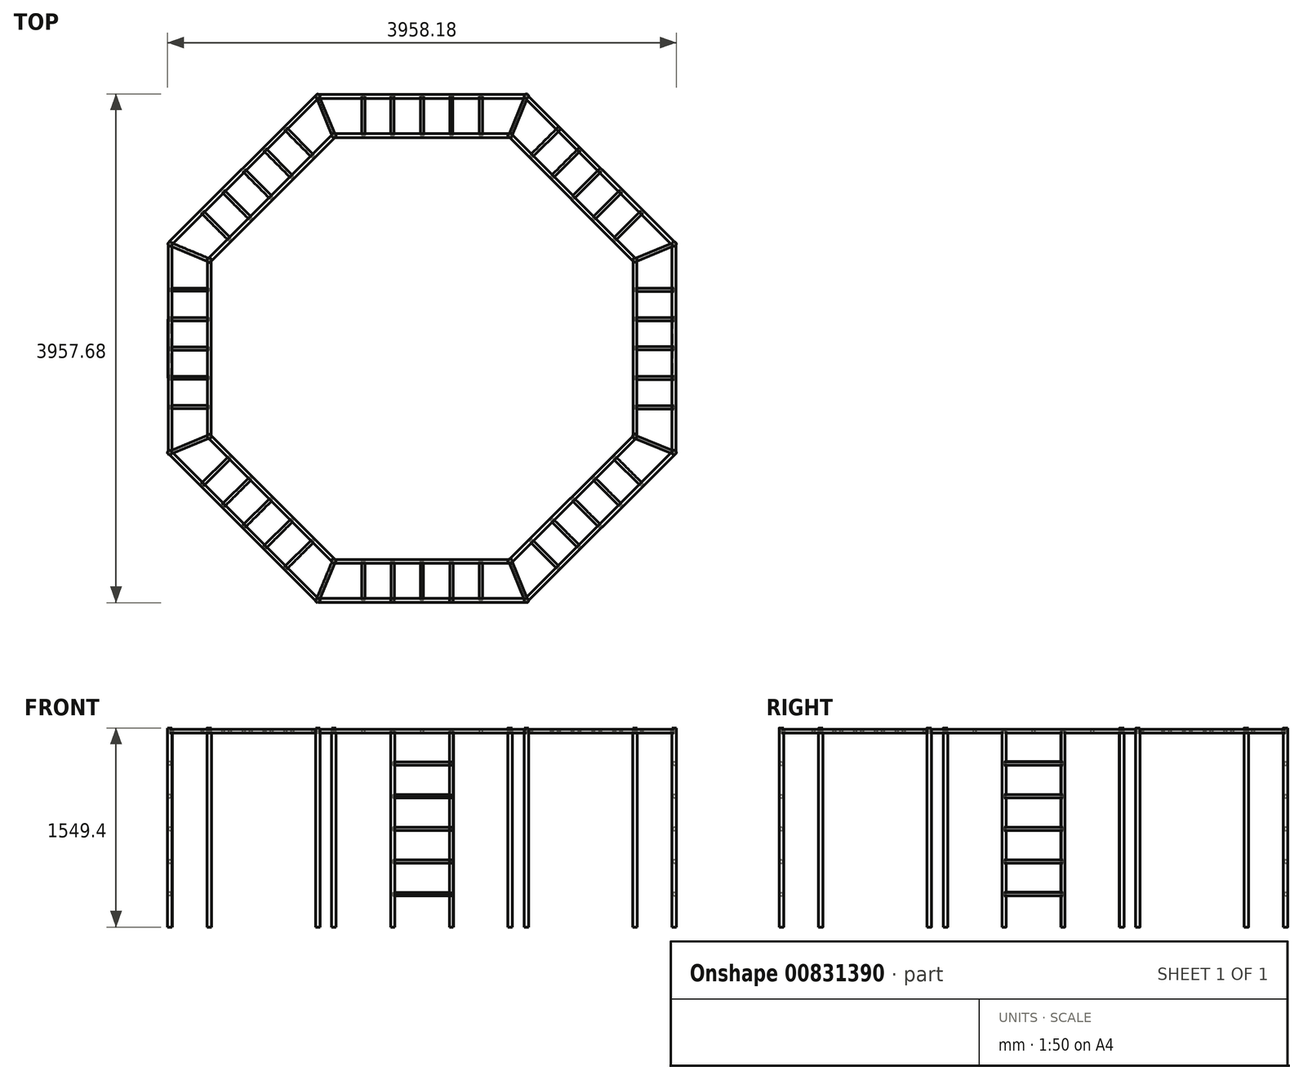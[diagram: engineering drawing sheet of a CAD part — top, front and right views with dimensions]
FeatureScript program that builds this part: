
annotation { "Feature Type Name" : "Feature", "Feature Type Description" : "" }
export const myFeature = defineFeature(function(context is Context, id is Id, definition is map)
    precondition{}
    {
        {
            var Q0;
            Q0=qCreatedBy(makeId("Top.planeOp"),FACE);
            var sketch = newSketch(context, id + "F0", { "sketchPlane" : qUnion([Q0])});
            skLineSegment(sketch, "E0", {"start": v(0, 0) * mm, "end": v(1624.1, 0) * mm});
            skLineSegment(sketch, "E1", {"start": v(1624.1, 0) * mm, "end": v(2772.51, 1148.41) * mm});
            skLineSegment(sketch, "E2", {"start": v(2772.51, 1148.41) * mm, "end": v(2772.51, 2772.51) * mm});
            skLineSegment(sketch, "E3", {"start": v(2772.51, 2772.51) * mm, "end": v(1624.1, 3920.92) * mm});
            skLineSegment(sketch, "E4", {"start": v(1624.1, 3920.92) * mm, "end": v(0, 3920.92) * mm});
            skLineSegment(sketch, "E5", {"start": v(0, 3920.92) * mm, "end": v(-1148.41, 2772.51) * mm});
            skLineSegment(sketch, "E6", {"start": v(-1148.41, 2772.51) * mm, "end": v(-1148.41, 1148.41) * mm});
            skLineSegment(sketch, "E7", {"start": v(-1148.41, 1148.41) * mm, "end": v(0, 0) * mm});
            skLineSegment(sketch, "E8", {"start": v(0, 0) * mm, "end": v(126.25, 304.79) * mm});
            skLineSegment(sketch, "E9", {"start": v(1624.1, 0) * mm, "end": v(1497.85, 304.79) * mm});
            skLineSegment(sketch, "E10", {"start": v(126.25, 304.79) * mm, "end": v(354.85, 304.79) * mm});
            skLineSegment(sketch, "E11", {"start": v(354.85, 304.79) * mm, "end": v(583.45, 304.79) * mm});
            skLineSegment(sketch, "E12", {"start": v(583.45, 304.79) * mm, "end": v(812.05, 304.79) * mm});
            skLineSegment(sketch, "E13", {"start": v(812.05, 304.79) * mm, "end": v(1040.65, 304.79) * mm});
            skLineSegment(sketch, "E14", {"start": v(1040.65, 304.79) * mm, "end": v(1269.25, 304.79) * mm});
            skLineSegment(sketch, "E15", {"start": v(1269.25, 304.79) * mm, "end": v(1497.85, 304.79) * mm});
            skLineSegment(sketch, "E16", {"start": v(354.85, 304.79) * mm, "end": v(354.85, 0) * mm});
            skLineSegment(sketch, "E17", {"start": v(583.45, 304.79) * mm, "end": v(583.45, 0) * mm});
            skLineSegment(sketch, "E18", {"start": v(812.05, 304.79) * mm, "end": v(812.05, 0) * mm});
            skLineSegment(sketch, "E19", {"start": v(1040.65, 304.79) * mm, "end": v(1040.65, 0) * mm});
            skLineSegment(sketch, "E20", {"start": v(1269.25, 304.79) * mm, "end": v(1269.25, 0) * mm});
            skLineSegment(sketch, "E21", {"start": v(2772.51, 1148.41) * mm, "end": v(2467.72, 1274.66) * mm});
            skLineSegment(sketch, "E22", {"start": v(1497.85, 304.79) * mm, "end": v(1659.5, 466.43) * mm});
            skLineSegment(sketch, "E23", {"start": v(1659.5, 466.43) * mm, "end": v(1821.14, 628.08) * mm});
            skLineSegment(sketch, "E24", {"start": v(1821.14, 628.08) * mm, "end": v(1982.79, 789.72) * mm});
            skLineSegment(sketch, "E25", {"start": v(1982.79, 789.72) * mm, "end": v(2144.43, 951.37) * mm});
            skLineSegment(sketch, "E26", {"start": v(2144.43, 951.37) * mm, "end": v(2306.08, 1113.01) * mm});
            skLineSegment(sketch, "E27", {"start": v(2306.08, 1113.01) * mm, "end": v(2467.72, 1274.66) * mm});
            skLineSegment(sketch, "E28", {"start": v(1659.5, 466.43) * mm, "end": v(1875.01, 250.91) * mm});
            skLineSegment(sketch, "E29", {"start": v(1821.14, 628.08) * mm, "end": v(2036.66, 412.56) * mm});
            skLineSegment(sketch, "E30", {"start": v(1982.79, 789.72) * mm, "end": v(2198.3, 574.2) * mm});
            skLineSegment(sketch, "E31", {"start": v(2144.43, 951.37) * mm, "end": v(2359.95, 735.85) * mm});
            skLineSegment(sketch, "E32", {"start": v(2306.08, 1113.01) * mm, "end": v(2521.6, 897.5) * mm});
            skLineSegment(sketch, "E33", {"start": v(2772.51, 2772.51) * mm, "end": v(2467.72, 2646.26) * mm});
            skLineSegment(sketch, "E34", {"start": v(2467.72, 2646.26) * mm, "end": v(2467.72, 2417.66) * mm});
            skLineSegment(sketch, "E35", {"start": v(2467.72, 2417.66) * mm, "end": v(2467.72, 2189.06) * mm});
            skLineSegment(sketch, "E36", {"start": v(2467.72, 2189.06) * mm, "end": v(2467.72, 1960.46) * mm});
            skLineSegment(sketch, "E37", {"start": v(2467.72, 1960.46) * mm, "end": v(2467.72, 1731.86) * mm});
            skLineSegment(sketch, "E38", {"start": v(2467.72, 1731.86) * mm, "end": v(2467.72, 1503.26) * mm});
            skLineSegment(sketch, "E39", {"start": v(2467.72, 1503.26) * mm, "end": v(2467.72, 1274.66) * mm});
            skLineSegment(sketch, "E40", {"start": v(2467.72, 1503.26) * mm, "end": v(2772.51, 1503.26) * mm});
            skLineSegment(sketch, "E41", {"start": v(2467.72, 1731.86) * mm, "end": v(2772.51, 1731.86) * mm});
            skLineSegment(sketch, "E42", {"start": v(2467.72, 1960.46) * mm, "end": v(2772.51, 1960.46) * mm});
            skLineSegment(sketch, "E43", {"start": v(2467.72, 2189.06) * mm, "end": v(2772.51, 2189.06) * mm});
            skLineSegment(sketch, "E44", {"start": v(2467.72, 2417.66) * mm, "end": v(2772.51, 2417.66) * mm});
            skLineSegment(sketch, "E45", {"start": v(1624.1, 3920.92) * mm, "end": v(1497.85, 3616.14) * mm});
            skLineSegment(sketch, "E46", {"start": v(2467.72, 2646.26) * mm, "end": v(2306.08, 2807.9) * mm});
            skLineSegment(sketch, "E47", {"start": v(2306.08, 2807.9) * mm, "end": v(2144.44, 2969.55) * mm});
            skLineSegment(sketch, "E48", {"start": v(2144.44, 2969.55) * mm, "end": v(1982.8, 3131.2) * mm});
            skLineSegment(sketch, "E49", {"start": v(1982.8, 3131.2) * mm, "end": v(1821.15, 3292.84) * mm});
            skLineSegment(sketch, "E50", {"start": v(1821.15, 3292.84) * mm, "end": v(1659.5, 3454.49) * mm});
            skLineSegment(sketch, "E51", {"start": v(1659.5, 3454.49) * mm, "end": v(1497.85, 3616.14) * mm});
            skLineSegment(sketch, "E52", {"start": v(2306.08, 2807.9) * mm, "end": v(2521.6, 3023.43) * mm});
            skLineSegment(sketch, "E53", {"start": v(2144.44, 2969.55) * mm, "end": v(2359.95, 3185.07) * mm});
            skLineSegment(sketch, "E54", {"start": v(1982.8, 3131.2) * mm, "end": v(2198.3, 3346.72) * mm});
            skLineSegment(sketch, "E55", {"start": v(1821.15, 3292.84) * mm, "end": v(2036.66, 3508.36) * mm});
            skLineSegment(sketch, "E56", {"start": v(1659.5, 3454.49) * mm, "end": v(1875.02, 3670) * mm});
            skLineSegment(sketch, "E57.MirrorCS", {"start": v(126.25, 304.79) * mm, "end": v(-35.4, 466.43) * mm});
            skLineSegment(sketch, "E58.MirrorCS", {"start": v(-35.4, 466.43) * mm, "end": v(-250.91, 250.91) * mm});
            skLineSegment(sketch, "E59.MirrorCS", {"start": v(-35.4, 466.43) * mm, "end": v(-197.04, 628.08) * mm});
            skLineSegment(sketch, "E60.MirrorCS", {"start": v(-197.04, 628.08) * mm, "end": v(-358.69, 789.72) * mm});
            skLineSegment(sketch, "E61.MirrorCS", {"start": v(-358.69, 789.72) * mm, "end": v(-520.33, 951.37) * mm});
            skLineSegment(sketch, "E62.MirrorCS", {"start": v(-681.98, 1113.01) * mm, "end": v(-843.62, 1274.66) * mm});
            skLineSegment(sketch, "E63.MirrorCS", {"start": v(-520.33, 951.37) * mm, "end": v(-681.98, 1113.01) * mm});
            skLineSegment(sketch, "E64.MirrorCS", {"start": v(-1148.41, 1148.41) * mm, "end": v(-843.62, 1274.66) * mm});
            skLineSegment(sketch, "E65.MirrorCS", {"start": v(-681.98, 1113.01) * mm, "end": v(-897.5, 897.5) * mm});
            skLineSegment(sketch, "E66.MirrorCS", {"start": v(-520.33, 951.37) * mm, "end": v(-735.85, 735.85) * mm});
            skLineSegment(sketch, "E67.MirrorCS", {"start": v(-358.69, 789.72) * mm, "end": v(-574.2, 574.2) * mm});
            skLineSegment(sketch, "E68.MirrorCS", {"start": v(-197.04, 628.08) * mm, "end": v(-412.56, 412.56) * mm});
            skLineSegment(sketch, "E69.MirrorCS", {"start": v(-843.62, 1274.66) * mm, "end": v(-843.62, 1503.26) * mm});
            skLineSegment(sketch, "E70.MirrorCS", {"start": v(-843.62, 1503.26) * mm, "end": v(-843.62, 1731.86) * mm});
            skLineSegment(sketch, "E71.MirrorCS", {"start": v(-843.62, 1731.86) * mm, "end": v(-843.62, 1960.46) * mm});
            skLineSegment(sketch, "E72.MirrorCS", {"start": v(-843.62, 1960.46) * mm, "end": v(-843.62, 2189.06) * mm});
            skLineSegment(sketch, "E73.MirrorCS", {"start": v(-843.62, 2189.06) * mm, "end": v(-843.62, 2417.66) * mm});
            skLineSegment(sketch, "E74.MirrorCS", {"start": v(-843.62, 2417.66) * mm, "end": v(-843.62, 2646.26) * mm});
            skLineSegment(sketch, "E75.MirrorCS", {"start": v(-1148.41, 2772.51) * mm, "end": v(-843.62, 2646.26) * mm});
            skLineSegment(sketch, "E76.MirrorCS", {"start": v(-843.62, 2417.66) * mm, "end": v(-1148.41, 2417.66) * mm});
            skLineSegment(sketch, "E77.MirrorCS", {"start": v(-843.62, 2189.06) * mm, "end": v(-1148.41, 2189.06) * mm});
            skLineSegment(sketch, "E78.MirrorCS", {"start": v(-843.62, 1960.46) * mm, "end": v(-1148.41, 1960.46) * mm});
            skLineSegment(sketch, "E79.MirrorCS", {"start": v(-843.62, 1731.86) * mm, "end": v(-1148.41, 1731.86) * mm});
            skLineSegment(sketch, "E80.MirrorCS", {"start": v(-843.62, 1503.26) * mm, "end": v(-1148.41, 1503.26) * mm});
            skLineSegment(sketch, "E81.MirrorCS", {"start": v(-681.98, 2807.91) * mm, "end": v(-843.62, 2646.26) * mm});
            skLineSegment(sketch, "E82.MirrorCS", {"start": v(-520.33, 2969.56) * mm, "end": v(-681.98, 2807.91) * mm});
            skLineSegment(sketch, "E83.MirrorCS", {"start": v(-358.69, 3131.2) * mm, "end": v(-520.33, 2969.56) * mm});
            skLineSegment(sketch, "E84.MirrorCS", {"start": v(-197.04, 3292.85) * mm, "end": v(-358.69, 3131.2) * mm});
            skLineSegment(sketch, "E85.MirrorCS", {"start": v(-35.4, 3454.5) * mm, "end": v(-197.04, 3292.85) * mm});
            skLineSegment(sketch, "E86.MirrorCS", {"start": v(126.25, 3616.14) * mm, "end": v(-35.4, 3454.5) * mm});
            skLineSegment(sketch, "E87.MirrorCS", {"start": v(0, 3920.92) * mm, "end": v(126.25, 3616.14) * mm});
            skLineSegment(sketch, "E88.MirrorCS", {"start": v(-35.4, 3454.5) * mm, "end": v(-250.91, 3670) * mm});
            skLineSegment(sketch, "E89.MirrorCS", {"start": v(-197.04, 3292.85) * mm, "end": v(-412.56, 3508.36) * mm});
            skLineSegment(sketch, "E90.MirrorCS", {"start": v(-358.69, 3131.2) * mm, "end": v(-574.2, 3346.72) * mm});
            skLineSegment(sketch, "E91.MirrorCS", {"start": v(-520.33, 2969.56) * mm, "end": v(-735.85, 3185.08) * mm});
            skLineSegment(sketch, "E92.MirrorCS", {"start": v(-681.98, 2807.91) * mm, "end": v(-897.5, 3023.43) * mm});
            skLineSegment(sketch, "E93.MirrorCS", {"start": v(126.25, 3616.14) * mm, "end": v(354.85, 3616.14) * mm});
            skLineSegment(sketch, "E94.MirrorCS", {"start": v(354.85, 3616.14) * mm, "end": v(583.45, 3616.14) * mm});
            skLineSegment(sketch, "E95.MirrorCS", {"start": v(583.45, 3616.14) * mm, "end": v(812.05, 3616.14) * mm});
            skLineSegment(sketch, "E96.MirrorCS", {"start": v(812.05, 3616.14) * mm, "end": v(1040.65, 3616.14) * mm});
            skLineSegment(sketch, "E97.MirrorCS", {"start": v(1040.65, 3616.14) * mm, "end": v(1269.25, 3616.14) * mm});
            skLineSegment(sketch, "E98.MirrorCS", {"start": v(1269.25, 3616.14) * mm, "end": v(1497.85, 3616.14) * mm});
            skLineSegment(sketch, "E99.MirrorCS", {"start": v(1269.25, 3616.14) * mm, "end": v(1269.25, 3920.92) * mm});
            skLineSegment(sketch, "E100.MirrorCS", {"start": v(1040.65, 3616.14) * mm, "end": v(1040.65, 3920.92) * mm});
            skLineSegment(sketch, "E101.MirrorCS", {"start": v(812.05, 3616.14) * mm, "end": v(812.05, 3920.92) * mm});
            skLineSegment(sketch, "E102.MirrorCS", {"start": v(583.45, 3616.14) * mm, "end": v(583.45, 3920.92) * mm});
            skLineSegment(sketch, "E103.MirrorCS", {"start": v(354.85, 3616.14) * mm, "end": v(354.85, 3920.92) * mm});
            skSolve(sketch);
        }
        {
            var Q0;
            Q0=sQuery(id+"F0.wireOp",VERTEX,"E0.start");
            var Q1;
            Q1=sQuery(id+"F0.wireOp",EDGE,"E7");
            cPlane(context, id + "F1", {"entities" : qUnion([Q0, Q1]), "cplaneType" : CPlaneType.LINE_POINT, "offset" : 25.4 * mm, "width" : 152.4 * mm, "height" : 152.4 * mm});
        }
        {
            var Q0;
            Q0=sQuery(id+"F0.wireOp",VERTEX,"E6.end");
            var Q1;
            Q1=sQuery(id+"F0.wireOp",EDGE,"E7");
            cPlane(context, id + "F2", {"entities" : qUnion([Q0, Q1]), "cplaneType" : CPlaneType.LINE_POINT, "offset" : 25.4 * mm, "width" : 152.4 * mm, "height" : 152.4 * mm});
        }
        {
            var Q0;
            Q0=sQuery(id+"F0.wireOp",VERTEX,"E0.end");
            var Q1;
            Q1=sQuery(id+"F0.wireOp",EDGE,"E1");
            cPlane(context, id + "F3", {"entities" : qUnion([Q0, Q1]), "cplaneType" : CPlaneType.LINE_POINT, "offset" : 25.4 * mm, "width" : 152.4 * mm, "height" : 152.4 * mm});
        }
        {
            var Q0;
            Q0=sQuery(id+"F0.wireOp",VERTEX,"E1.end");
            var Q1;
            Q1=sQuery(id+"F0.wireOp",EDGE,"E1");
            cPlane(context, id + "F4", {"entities" : qUnion([Q0, Q1]), "cplaneType" : CPlaneType.LINE_POINT, "offset" : 25.4 * mm, "width" : 152.4 * mm, "height" : 152.4 * mm});
        }
        {
            var Q0;
            Q0=sQuery(id+"F0.wireOp",VERTEX,"E71.MirrorCS.end");
            var Q1;
            Q1=sQuery(id+"F0.wireOp",EDGE,"E78.MirrorCS");
            cPlane(context, id + "F5", {"entities" : qUnion([Q0, Q1]), "cplaneType" : CPlaneType.LINE_POINT, "offset" : 25.4 * mm, "width" : 152.4 * mm, "height" : 152.4 * mm});
        }
        {
            var Q0;
            Q0=qCreatedBy(id+"F5.planeOp",FACE);
            var sketch = newSketch(context, id + "F6", { "sketchPlane" : qUnion([Q0])});
            skLineSegment(sketch, "E104", {"start": v(-1274.16, 0) * mm, "end": v(-1274.16, -1524) * mm});
            skLineSegment(sketch, "E105", {"start": v(-2645.18, 0) * mm, "end": v(-2645.18, -1524) * mm});
            skSolve(sketch);
        }
        {
            var Q0;
            Q0=sQuery(id+"F0.wireOp",VERTEX,"E95.MirrorCS.end");
            var Q1;
            Q1=sQuery(id+"F0.wireOp",EDGE,"E101.MirrorCS");
            cPlane(context, id + "F7", {"entities" : qUnion([Q0, Q1]), "cplaneType" : CPlaneType.LINE_POINT, "offset" : 25.4 * mm, "width" : 152.4 * mm, "height" : 152.4 * mm});
        }
        {
            var Q0;
            Q0=sQuery(id+"F0.wireOp",VERTEX,"E12.end");
            var Q1;
            Q1=sQuery(id+"F0.wireOp",EDGE,"E18");
            cPlane(context, id + "F8", {"entities" : qUnion([Q0, Q1]), "cplaneType" : CPlaneType.LINE_POINT, "offset" : 25.4 * mm, "width" : 152.4 * mm, "height" : 152.4 * mm});
        }
        {
            var Q0;
            Q0=sQuery(id+"F0.wireOp",VERTEX,"E36.end");
            var Q1;
            Q1=sQuery(id+"F0.wireOp",EDGE,"E42");
            cPlane(context, id + "F9", {"entities" : qUnion([Q0, Q1]), "cplaneType" : CPlaneType.LINE_POINT, "offset" : 25.4 * mm, "width" : 152.4 * mm, "height" : 152.4 * mm});
        }
        {
            var Q0;
            Q0=sQuery(id+"F0.wireOp",EDGE,"E0");
            cPoint(context, id + "F10", {"entities" : qUnion([Q0]), "parameter" : 0.5});
        }
        {
            var Q0;
            Q0 = qCreatedBy(id + "F10" ,VERTEX);
            var Q1;
            Q1=sQuery(id+"F0.wireOp",EDGE,"E18");
            cPlane(context, id + "F11", {"entities" : qUnion([Q0, Q1]), "cplaneType" : CPlaneType.LINE_POINT, "offset" : 25.4 * mm, "width" : 152.4 * mm, "height" : 152.4 * mm});
        }
        {
            var Q0;
            Q0=sQuery(id+"F0.wireOp",EDGE,"E2");
            cPoint(context, id + "F12", {"entities" : qUnion([Q0]), "parameter" : 0.5});
        }
        {
            var Q0;
            Q0 = qCreatedBy(id + "F12" ,VERTEX);
            var Q1;
            Q1=sQuery(id+"F0.wireOp",EDGE,"E42");
            cPlane(context, id + "F13", {"entities" : qUnion([Q0, Q1]), "cplaneType" : CPlaneType.LINE_POINT, "offset" : 25.4 * mm, "width" : 152.4 * mm, "height" : 152.4 * mm});
        }
        {
            var Q0;
            Q0=sQuery(id+"F0.wireOp",EDGE,"E4");
            cPoint(context, id + "F14", {"entities" : qUnion([Q0]), "parameter" : 0.5});
        }
        {
            var Q0;
            Q0 = qCreatedBy(id + "F14" ,VERTEX);
            var Q1;
            Q1=sQuery(id+"F0.wireOp",EDGE,"E101.MirrorCS");
            cPlane(context, id + "F15", {"entities" : qUnion([Q0, Q1]), "cplaneType" : CPlaneType.LINE_POINT, "offset" : 25.4 * mm, "width" : 152.4 * mm, "height" : 152.4 * mm});
        }
        {
            var Q0;
            Q0=sQuery(id+"F0.wireOp",EDGE,"E6");
            cPoint(context, id + "F16", {"entities" : qUnion([Q0]), "parameter" : 0.5});
        }
        {
            var Q0;
            Q0 = qCreatedBy(id + "F16" ,VERTEX);
            var Q1;
            Q1=sQuery(id+"F0.wireOp",EDGE,"E78.MirrorCS");
            cPlane(context, id + "F17", {"entities" : qUnion([Q0, Q1]), "cplaneType" : CPlaneType.LINE_POINT, "offset" : 25.4 * mm, "width" : 152.4 * mm, "height" : 152.4 * mm});
        }
        {
            var Q0;
            Q0=qCreatedBy(id+"F1.planeOp",FACE);
            var sketch = newSketch(context, id + "F18", { "sketchPlane" : qUnion([Q0])});
            skCircle(sketch, "E106", {"center": v(0, 0) * mm, "radius": 15 * mm});
            skSolve(sketch);
        }
        {
            var Q0;
            Q0=makeQuery(id+"F18.imprint","IMPRINT",FACE,{"disambiguationData":[TD([[makeQuery(id+"F18.imprint","IMPRINT",EDGE,{"derivedFrom":sQuery(id+"F18.wireOp",EDGE,"E106")}),1.0]])]});
            extrude(context, id + "F19", {"entities" : qUnion([Q0]), "oppositeDirection" : true, "depth" : 1624.1 * mm, "offsetDistance" : 25.4 * mm});
        }
        {
            var Q0;
            Q0=qCreatedBy(makeId("Right.planeOp"),FACE);
            var sketch = newSketch(context, id + "F20", { "sketchPlane" : qUnion([Q0])});
            skCircle(sketch, "E107", {"center": v(0, 0) * mm, "radius": 15 * mm});
            skSolve(sketch);
        }
        {
            var Q0;
            Q0=makeQuery(id+"F20.imprint","IMPRINT",FACE,{"disambiguationData":[TD([[makeQuery(id+"F20.imprint","IMPRINT",EDGE,{"derivedFrom":sQuery(id+"F20.wireOp",EDGE,"E107")}),1.0]])]});
            extrude(context, id + "F21", {"entities" : qUnion([Q0]), "operationType" : NewBodyOperationType.ADD, "depth" : 1624.1 * mm, "offsetDistance" : 25.4 * mm});
        }
        {
            var Q0;
            Q0=sQuery(id+"F0.wireOp",VERTEX,"E6.end");
            var Q1;
            Q1=sQuery(id+"F0.wireOp",EDGE,"E6");
            cPlane(context, id + "F22", {"entities" : qUnion([Q0, Q1]), "cplaneType" : CPlaneType.LINE_POINT, "offset" : 25.4 * mm, "width" : 152.4 * mm, "height" : 152.4 * mm});
        }
        {
            var Q0;
            Q0=qCreatedBy(id+"F22.planeOp",FACE);
            var sketch = newSketch(context, id + "F23", { "sketchPlane" : qUnion([Q0])});
            skCircle(sketch, "E108", {"center": v(-1147.47, 0) * mm, "radius": 15 * mm});
            skSolve(sketch);
        }
        {
            var Q0;
            Q0=makeQuery(id+"F23.imprint","IMPRINT",FACE,{"disambiguationData":[TD([[makeQuery(id+"F23.imprint","IMPRINT",EDGE,{"derivedFrom":sQuery(id+"F23.wireOp",EDGE,"E108")}),1.0]])]});
            extrude(context, id + "F24", {"entities" : qUnion([Q0]), "operationType" : NewBodyOperationType.ADD, "oppositeDirection" : true, "depth" : 1624.1 * mm, "offsetDistance" : 25.4 * mm});
        }
        {
            var Q0;
            Q0=sQuery(id+"F0.wireOp",VERTEX,"E5.end");
            var Q1;
            Q1=sQuery(id+"F0.wireOp",EDGE,"E5");
            cPlane(context, id + "F25", {"entities" : qUnion([Q0, Q1]), "cplaneType" : CPlaneType.LINE_POINT, "offset" : 25.4 * mm, "width" : 152.4 * mm, "height" : 152.4 * mm});
        }
        {
            var Q0;
            Q0=qCreatedBy(id+"F25.planeOp",FACE);
            var sketch = newSketch(context, id + "F26", { "sketchPlane" : qUnion([Q0])});
            skCircle(sketch, "E109", {"center": v(-2774.05, 0) * mm, "radius": 15 * mm});
            skSolve(sketch);
        }
        {
            var Q0;
            Q0=makeQuery(id+"F26.imprint","IMPRINT",FACE,{"disambiguationData":[TD([[makeQuery(id+"F26.imprint","IMPRINT",EDGE,{"derivedFrom":sQuery(id+"F26.wireOp",EDGE,"E109")}),1.0]])]});
            extrude(context, id + "F27", {"entities" : qUnion([Q0]), "operationType" : NewBodyOperationType.ADD, "oppositeDirection" : true, "depth" : 1624.1 * mm, "offsetDistance" : 25.4 * mm});
        }
        {
            var Q0;
            Q0=sQuery(id+"F0.wireOp",VERTEX,"E4.end");
            var Q1;
            Q1=sQuery(id+"F0.wireOp",EDGE,"E4");
            cPlane(context, id + "F28", {"entities" : qUnion([Q0, Q1]), "cplaneType" : CPlaneType.LINE_POINT, "offset" : 25.4 * mm, "width" : 152.4 * mm, "height" : 152.4 * mm});
        }
        {
            var Q0;
            Q0=qCreatedBy(id+"F28.planeOp",FACE);
            var sketch = newSketch(context, id + "F29", { "sketchPlane" : qUnion([Q0])});
            skCircle(sketch, "E110", {"center": v(-3920.97, 0) * mm, "radius": 15 * mm});
            skSolve(sketch);
        }
        {
            var Q0;
            Q0=makeQuery(id+"F29.imprint","IMPRINT",FACE,{"disambiguationData":[TD([[makeQuery(id+"F29.imprint","IMPRINT",EDGE,{"derivedFrom":sQuery(id+"F29.wireOp",EDGE,"E110")}),1.0]])]});
            extrude(context, id + "F30", {"entities" : qUnion([Q0]), "operationType" : NewBodyOperationType.ADD, "oppositeDirection" : true, "depth" : 1624.1 * mm, "offsetDistance" : 25.4 * mm});
        }
        {
            var Q0;
            Q0=sQuery(id+"F0.wireOp",VERTEX,"E3.end");
            var Q1;
            Q1=sQuery(id+"F0.wireOp",EDGE,"E3");
            cPlane(context, id + "F31", {"entities" : qUnion([Q0, Q1]), "cplaneType" : CPlaneType.LINE_POINT, "offset" : 25.4 * mm, "width" : 152.4 * mm, "height" : 152.4 * mm});
        }
        {
            var Q0;
            Q0=qCreatedBy(id+"F31.planeOp",FACE);
            var sketch = newSketch(context, id + "F32", { "sketchPlane" : qUnion([Q0])});
            skCircle(sketch, "E111", {"center": v(-3919.06, 0) * mm, "radius": 15 * mm});
            skSolve(sketch);
        }
        {
            var Q0;
            Q0=makeQuery(id+"F32.imprint","IMPRINT",FACE,{"disambiguationData":[TD([[makeQuery(id+"F32.imprint","IMPRINT",EDGE,{"derivedFrom":sQuery(id+"F32.wireOp",EDGE,"E111")}),1.0]])]});
            extrude(context, id + "F33", {"entities" : qUnion([Q0]), "operationType" : NewBodyOperationType.ADD, "oppositeDirection" : true, "depth" : 1624.1 * mm, "offsetDistance" : 25.4 * mm});
        }
        {
            var Q0;
            Q0=sQuery(id+"F0.wireOp",VERTEX,"E2.end");
            var Q1;
            Q1=sQuery(id+"F0.wireOp",EDGE,"E2");
            cPlane(context, id + "F34", {"entities" : qUnion([Q0, Q1]), "cplaneType" : CPlaneType.LINE_POINT, "offset" : 25.4 * mm, "width" : 152.4 * mm, "height" : 152.4 * mm});
        }
        {
            var Q0;
            Q0=qCreatedBy(id+"F34.planeOp",FACE);
            var sketch = newSketch(context, id + "F35", { "sketchPlane" : qUnion([Q0])});
            skCircle(sketch, "E112", {"center": v(-2771.97, 0) * mm, "radius": 15 * mm});
            skSolve(sketch);
        }
        {
            var Q0;
            Q0=makeQuery(id+"F35.imprint","IMPRINT",FACE,{"disambiguationData":[TD([[makeQuery(id+"F35.imprint","IMPRINT",EDGE,{"derivedFrom":sQuery(id+"F35.wireOp",EDGE,"E112")}),1.0]])]});
            extrude(context, id + "F36", {"entities" : qUnion([Q0]), "operationType" : NewBodyOperationType.ADD, "oppositeDirection" : true, "depth" : 1624.1 * mm, "offsetDistance" : 25.4 * mm});
        }
        {
            var Q0;
            Q0=qCreatedBy(id+"F3.planeOp",FACE);
            var sketch = newSketch(context, id + "F37", { "sketchPlane" : qUnion([Q0])});
            skCircle(sketch, "E113", {"center": v(-1146.74, 0) * mm, "radius": 15 * mm});
            skSolve(sketch);
        }
        {
            var Q0;
            Q0=makeQuery(id+"F37.imprint","IMPRINT",FACE,{"disambiguationData":[TD([[makeQuery(id+"F37.imprint","IMPRINT",EDGE,{"derivedFrom":sQuery(id+"F37.wireOp",EDGE,"E113")}),1.0]])]});
            extrude(context, id + "F38", {"entities" : qUnion([Q0]), "operationType" : NewBodyOperationType.ADD, "depth" : 1624.1 * mm, "offsetDistance" : 25.4 * mm});
        }
        {
            var Q0;
            Q0=sQuery(id+"F0.wireOp",VERTEX,"E8.end");
            var Q1;
            Q1=sQuery(id+"F0.wireOp",EDGE,"E57.MirrorCS");
            cPlane(context, id + "F39", {"entities" : qUnion([Q0, Q1]), "cplaneType" : CPlaneType.LINE_POINT, "offset" : 25.4 * mm, "width" : 152.4 * mm, "height" : 152.4 * mm});
        }
        {
            var Q0;
            Q0=qCreatedBy(id+"F39.planeOp",FACE);
            var sketch = newSketch(context, id + "F40", { "sketchPlane" : qUnion([Q0])});
            skCircle(sketch, "E114", {"center": v(-304.82, 0) * mm, "radius": 15 * mm});
            skSolve(sketch);
        }
        {
            var Q0;
            Q0=makeQuery(id+"F40.imprint","IMPRINT",FACE,{"disambiguationData":[TD([[makeQuery(id+"F40.imprint","IMPRINT",EDGE,{"derivedFrom":sQuery(id+"F40.wireOp",EDGE,"E114")}),1.0]])]});
            extrude(context, id + "F41", {"entities" : qUnion([Q0]), "depth" : 1371.6 * mm, "offsetDistance" : 25.4 * mm});
        }
        {
            var Q0;
            Q0=sQuery(id+"F0.wireOp",VERTEX,"E62.MirrorCS.end");
            var Q1;
            Q1=sQuery(id+"F0.wireOp",EDGE,"E69.MirrorCS");
            cPlane(context, id + "F42", {"entities" : qUnion([Q0, Q1]), "cplaneType" : CPlaneType.LINE_POINT, "offset" : 25.4 * mm, "width" : 152.4 * mm, "height" : 152.4 * mm});
        }
        {
            var Q0;
            Q0=qCreatedBy(id+"F42.planeOp",FACE);
            var sketch = newSketch(context, id + "F43", { "sketchPlane" : qUnion([Q0])});
            skCircle(sketch, "E115", {"center": v(843.67, 0) * mm, "radius": 15 * mm});
            skSolve(sketch);
        }
        {
            var Q0;
            Q0=makeQuery(id+"F43.imprint","IMPRINT",FACE,{"disambiguationData":[TD([[makeQuery(id+"F43.imprint","IMPRINT",EDGE,{"derivedFrom":sQuery(id+"F43.wireOp",EDGE,"E115")}),1.0]])]});
            extrude(context, id + "F44", {"entities" : qUnion([Q0]), "operationType" : NewBodyOperationType.ADD, "depth" : 1371.6 * mm, "offsetDistance" : 25.4 * mm});
        }
        {
            var Q0;
            Q0=sQuery(id+"F6.wireOp",VERTEX,"E105.start");
            var Q1;
            Q1=sQuery(id+"F0.wireOp",EDGE,"E81.MirrorCS");
            cPlane(context, id + "F45", {"entities" : qUnion([Q0, Q1]), "cplaneType" : CPlaneType.LINE_POINT, "offset" : 25.4 * mm, "width" : 152.4 * mm, "height" : 152.4 * mm});
        }
        {
            var Q0;
            Q0=qCreatedBy(id+"F45.planeOp",FACE);
            var sketch = newSketch(context, id + "F46", { "sketchPlane" : qUnion([Q0])});
            skCircle(sketch, "E116", {"center": v(-2467.6, 0) * mm, "radius": 15 * mm});
            skSolve(sketch);
        }
        {
            var Q0;
            Q0=makeQuery(id+"F46.imprint","IMPRINT",FACE,{"disambiguationData":[TD([[makeQuery(id+"F46.imprint","IMPRINT",EDGE,{"derivedFrom":sQuery(id+"F46.wireOp",EDGE,"E116")}),1.0]])]});
            extrude(context, id + "F47", {"entities" : qUnion([Q0]), "operationType" : NewBodyOperationType.ADD, "oppositeDirection" : true, "depth" : 1371.6 * mm, "offsetDistance" : 25.4 * mm});
        }
        {
            var Q0;
            Q0=sQuery(id+"F0.wireOp",VERTEX,"E86.MirrorCS.start");
            var Q1;
            Q1=sQuery(id+"F0.wireOp",EDGE,"E93.MirrorCS");
            cPlane(context, id + "F48", {"entities" : qUnion([Q0, Q1]), "cplaneType" : CPlaneType.LINE_POINT, "offset" : 25.4 * mm, "width" : 152.4 * mm, "height" : 152.4 * mm});
        }
        {
            var Q0;
            Q0=qCreatedBy(id+"F48.planeOp",FACE);
            var sketch = newSketch(context, id + "F49", { "sketchPlane" : qUnion([Q0])});
            skCircle(sketch, "E117", {"center": v(3616.57, 0) * mm, "radius": 15 * mm});
            skSolve(sketch);
        }
        {
            var Q0;
            Q0=makeQuery(id+"F49.imprint","IMPRINT",FACE,{"disambiguationData":[TD([[makeQuery(id+"F49.imprint","IMPRINT",EDGE,{"derivedFrom":sQuery(id+"F49.wireOp",EDGE,"E117")}),1.0]])]});
            extrude(context, id + "F50", {"entities" : qUnion([Q0]), "operationType" : NewBodyOperationType.ADD, "depth" : 1371.6 * mm, "offsetDistance" : 25.4 * mm});
        }
        {
            var Q0;
            Q0=sQuery(id+"F0.wireOp",VERTEX,"E45.end");
            var Q1;
            Q1=sQuery(id+"F0.wireOp",EDGE,"E51");
            cPlane(context, id + "F51", {"entities" : qUnion([Q0, Q1]), "cplaneType" : CPlaneType.LINE_POINT, "offset" : 25.4 * mm, "width" : 152.4 * mm, "height" : 152.4 * mm});
        }
        {
            var Q0;
            Q0=qCreatedBy(id+"F51.planeOp",FACE);
            var sketch = newSketch(context, id + "F52", { "sketchPlane" : qUnion([Q0])});
            skCircle(sketch, "E118", {"center": v(-3616.84, 0) * mm, "radius": 15 * mm});
            skSolve(sketch);
        }
        {
            var Q0;
            Q0=makeQuery(id+"F52.imprint","IMPRINT",FACE,{"disambiguationData":[TD([[makeQuery(id+"F52.imprint","IMPRINT",EDGE,{"derivedFrom":sQuery(id+"F52.wireOp",EDGE,"E118")}),1.0]])]});
            extrude(context, id + "F53", {"entities" : qUnion([Q0]), "operationType" : NewBodyOperationType.ADD, "oppositeDirection" : true, "depth" : 1371.6 * mm, "offsetDistance" : 25.4 * mm});
        }
        {
            var Q0;
            Q0=sQuery(id+"F0.wireOp",VERTEX,"E33.end");
            var Q1;
            Q1=sQuery(id+"F0.wireOp",EDGE,"E34");
            cPlane(context, id + "F54", {"entities" : qUnion([Q0, Q1]), "cplaneType" : CPlaneType.LINE_POINT, "offset" : 25.4 * mm, "width" : 152.4 * mm, "height" : 152.4 * mm});
        }
        {
            var Q0;
            Q0=qCreatedBy(id+"F54.planeOp",FACE);
            var sketch = newSketch(context, id + "F55", { "sketchPlane" : qUnion([Q0])});
            skCircle(sketch, "E119", {"center": v(2468.86, 0) * mm, "radius": 15 * mm});
            skSolve(sketch);
        }
        {
            var Q0;
            Q0=makeQuery(id+"F55.imprint","IMPRINT",FACE,{"disambiguationData":[TD([[makeQuery(id+"F55.imprint","IMPRINT",EDGE,{"derivedFrom":sQuery(id+"F55.wireOp",EDGE,"E119")}),1.0]])]});
            extrude(context, id + "F56", {"entities" : qUnion([Q0]), "operationType" : NewBodyOperationType.ADD, "depth" : 1371.6 * mm, "offsetDistance" : 25.4 * mm});
        }
        {
            var Q0;
            Q0=sQuery(id+"F0.wireOp",VERTEX,"E21.end");
            var Q1;
            Q1=sQuery(id+"F0.wireOp",EDGE,"E27");
            cPlane(context, id + "F57", {"entities" : qUnion([Q0, Q1]), "cplaneType" : CPlaneType.LINE_POINT, "offset" : 25.4 * mm, "width" : 152.4 * mm, "height" : 152.4 * mm});
        }
        {
            var Q0;
            Q0=qCreatedBy(id+"F57.planeOp",FACE);
            var sketch = newSketch(context, id + "F58", { "sketchPlane" : qUnion([Q0])});
            skCircle(sketch, "E120", {"center": v(-843.77, 0) * mm, "radius": 15 * mm});
            skSolve(sketch);
        }
        {
            var Q0;
            Q0=makeQuery(id+"F58.imprint","IMPRINT",FACE,{"disambiguationData":[TD([[makeQuery(id+"F58.imprint","IMPRINT",EDGE,{"derivedFrom":sQuery(id+"F58.wireOp",EDGE,"E120")}),1.0]])]});
            extrude(context, id + "F59", {"entities" : qUnion([Q0]), "operationType" : NewBodyOperationType.ADD, "oppositeDirection" : true, "depth" : 1371.6 * mm, "offsetDistance" : 25.4 * mm});
        }
        {
            var Q0;
            Q0=sQuery(id+"F0.wireOp",VERTEX,"E9.end");
            var Q1;
            Q1=sQuery(id+"F0.wireOp",EDGE,"E15");
            cPlane(context, id + "F60", {"entities" : qUnion([Q0, Q1]), "cplaneType" : CPlaneType.LINE_POINT, "offset" : 25.4 * mm, "width" : 152.4 * mm, "height" : 152.4 * mm});
        }
        {
            var Q0;
            Q0=qCreatedBy(id+"F60.planeOp",FACE);
            var sketch = newSketch(context, id + "F61", { "sketchPlane" : qUnion([Q0])});
            skCircle(sketch, "E121", {"center": v(303.61, 0) * mm, "radius": 15 * mm});
            skSolve(sketch);
        }
        {
            var Q0;
            Q0=makeQuery(id+"F61.imprint","IMPRINT",FACE,{"disambiguationData":[TD([[makeQuery(id+"F61.imprint","IMPRINT",EDGE,{"derivedFrom":sQuery(id+"F61.wireOp",EDGE,"E121")}),1.0]])]});
            extrude(context, id + "F62", {"entities" : qUnion([Q0]), "operationType" : NewBodyOperationType.ADD, "oppositeDirection" : true, "depth" : 1371.6 * mm, "offsetDistance" : 25.4 * mm});
        }
        {
            var Q0;
            Q0=qCreatedBy(id+"F8.planeOp",FACE);
            var sketch = newSketch(context, id + "F63", { "sketchPlane" : qUnion([Q0])});
            skCircle(sketch, "E122", {"center": v(354.16, 0) * mm, "radius": 12.5 * mm});
            skCircle(sketch, "E123", {"center": v(583.06, 0) * mm, "radius": 12.5 * mm});
            skCircle(sketch, "E124", {"center": v(810.79, 0) * mm, "radius": 12.5 * mm});
            skCircle(sketch, "E125", {"center": v(1039.86, 0) * mm, "radius": 12.5 * mm});
            skCircle(sketch, "E126", {"center": v(1268.74, 0) * mm, "radius": 12.5 * mm});
            skSolve(sketch);
        }
        {
            var Q0;
            Q0 = qSketchRegion(id + "F63", true);
            extrude(context, id + "F64", {"entities" : qUnion([Q0]), "depth" : 304.8 * mm, "offsetDistance" : 25.4 * mm});
        }
        {
            var Q0;
            Q0=sQuery(id+"F0.wireOp",VERTEX,"E60.MirrorCS.end");
            var Q1;
            Q1=sQuery(id+"F0.wireOp",EDGE,"E67.MirrorCS");
            cPlane(context, id + "F65", {"entities" : qUnion([Q0, Q1]), "cplaneType" : CPlaneType.LINE_POINT, "offset" : 25.4 * mm, "width" : 152.4 * mm, "height" : 152.4 * mm});
        }
        {
            var Q0;
            Q0=qCreatedBy(id+"F65.planeOp",FACE);
            var sketch = newSketch(context, id + "F66", { "sketchPlane" : qUnion([Q0])});
            skCircle(sketch, "E127", {"center": v(-1270, 0) * mm, "radius": 12.5 * mm});
            skCircle(sketch, "E128", {"center": v(-1041.5, 0) * mm, "radius": 12.5 * mm});
            skCircle(sketch, "E129", {"center": v(-812.71, 0) * mm, "radius": 12.5 * mm});
            skCircle(sketch, "E130", {"center": v(-583.09, 0) * mm, "radius": 12.5 * mm});
            skCircle(sketch, "E131", {"center": v(-354.3, 0) * mm, "radius": 12.5 * mm});
            skSolve(sketch);
        }
        {
            var Q0;
            Q0 = qSketchRegion(id + "F66", true);
            extrude(context, id + "F67", {"entities" : qUnion([Q0]), "depth" : 304.8 * mm, "offsetDistance" : 25.4 * mm});
        }
        {
            var Q0;
            Q0=qCreatedBy(id+"F5.planeOp",FACE);
            var sketch = newSketch(context, id + "F68", { "sketchPlane" : qUnion([Q0])});
            skCircle(sketch, "E132", {"center": v(-2417.82, 0) * mm, "radius": 12.5 * mm});
            skCircle(sketch, "E133", {"center": v(-2188.87, 0) * mm, "radius": 12.5 * mm});
            skCircle(sketch, "E134", {"center": v(-1959.93, 0) * mm, "radius": 12.5 * mm});
            skCircle(sketch, "E135", {"center": v(-1731.82, 0) * mm, "radius": 12.5 * mm});
            skCircle(sketch, "E136", {"center": v(-1503.71, 0) * mm, "radius": 12.5 * mm});
            skSolve(sketch);
        }
        {
            var Q0;
            Q0 = qSketchRegion(id + "F68", true);
            extrude(context, id + "F69", {"entities" : qUnion([Q0]), "depth" : 304.8 * mm, "offsetDistance" : 25.4 * mm});
        }
        {
            var Q0;
            Q0=sQuery(id+"F0.wireOp",VERTEX,"E83.MirrorCS.start");
            var Q1;
            Q1=sQuery(id+"F0.wireOp",EDGE,"E90.MirrorCS");
            cPlane(context, id + "F70", {"entities" : qUnion([Q0, Q1]), "cplaneType" : CPlaneType.LINE_POINT, "offset" : 25.4 * mm, "width" : 152.4 * mm, "height" : 152.4 * mm});
        }
        {
            var Q0;
            Q0=qCreatedBy(id+"F70.planeOp",FACE);
            var sketch = newSketch(context, id + "F71", { "sketchPlane" : qUnion([Q0])});
            skCircle(sketch, "E137", {"center": v(-2417.73, 0) * mm, "radius": 12.5 * mm});
            skCircle(sketch, "E138", {"center": v(-2188.56, 0) * mm, "radius": 12.5 * mm});
            skCircle(sketch, "E139", {"center": v(-1960.16, 0) * mm, "radius": 12.5 * mm});
            skCircle(sketch, "E140", {"center": v(-1731.76, 0) * mm, "radius": 12.5 * mm});
            skCircle(sketch, "E141", {"center": v(-1502.6, 0) * mm, "radius": 12.5 * mm});
            skSolve(sketch);
        }
        {
            var Q0;
            Q0 = qSketchRegion(id + "F71", true);
            extrude(context, id + "F72", {"entities" : qUnion([Q0]), "depth" : 304.8 * mm, "offsetDistance" : 25.4 * mm});
        }
        {
            var Q0;
            Q0=qCreatedBy(id+"F7.planeOp",FACE);
            var sketch = newSketch(context, id + "F73", { "sketchPlane" : qUnion([Q0])});
            skCircle(sketch, "E142", {"center": v(-1269.79, 0) * mm, "radius": 12.5 * mm});
            skCircle(sketch, "E143", {"center": v(-1039.7, 0) * mm, "radius": 12.5 * mm});
            skCircle(sketch, "E144", {"center": v(-812, 0) * mm, "radius": 12.5 * mm});
            skCircle(sketch, "E145", {"center": v(-581.91, 0) * mm, "radius": 12.5 * mm});
            skCircle(sketch, "E146", {"center": v(-354.2, 0) * mm, "radius": 12.5 * mm});
            skSolve(sketch);
        }
        {
            var Q0;
            Q0 = qSketchRegion(id + "F73", true);
            extrude(context, id + "F74", {"entities" : qUnion([Q0]), "depth" : 304.8 * mm, "offsetDistance" : 25.4 * mm});
        }
        {
            var Q0;
            Q0=sQuery(id+"F0.wireOp",VERTEX,"E48.end");
            var Q1;
            Q1=sQuery(id+"F0.wireOp",EDGE,"E54");
            cPlane(context, id + "F75", {"entities" : qUnion([Q0, Q1]), "cplaneType" : CPlaneType.LINE_POINT, "offset" : 25.4 * mm, "width" : 152.4 * mm, "height" : 152.4 * mm});
        }
        {
            var Q0;
            Q0=qCreatedBy(id+"F75.planeOp",FACE);
            var sketch = newSketch(context, id + "F76", { "sketchPlane" : qUnion([Q0])});
            skCircle(sketch, "E147", {"center": v(353.44, 0) * mm, "radius": 12.5 * mm});
            skCircle(sketch, "E148", {"center": v(583.1, 0) * mm, "radius": 12.5 * mm});
            skCircle(sketch, "E149", {"center": v(811.62, 0) * mm, "radius": 12.5 * mm});
            skCircle(sketch, "E150", {"center": v(1040.15, 0) * mm, "radius": 12.5 * mm});
            skCircle(sketch, "E151", {"center": v(1268.67, 0) * mm, "radius": 12.5 * mm});
            skSolve(sketch);
        }
        {
            var Q0;
            Q0 = qSketchRegion(id + "F76", true);
            extrude(context, id + "F77", {"entities" : qUnion([Q0]), "depth" : 304.8 * mm, "offsetDistance" : 25.4 * mm});
        }
        {
            var Q0;
            Q0=qCreatedBy(id+"F9.planeOp",FACE);
            var sketch = newSketch(context, id + "F78", { "sketchPlane" : qUnion([Q0])});
            skCircle(sketch, "E152", {"center": v(1502.59, 0) * mm, "radius": 12.5 * mm});
            skCircle(sketch, "E153", {"center": v(1730.86, 0) * mm, "radius": 12.5 * mm});
            skCircle(sketch, "E154", {"center": v(1960.88, 0) * mm, "radius": 12.5 * mm});
            skCircle(sketch, "E155", {"center": v(2187.4, 0) * mm, "radius": 12.5 * mm});
            skCircle(sketch, "E156", {"center": v(2417.42, 0) * mm, "radius": 12.5 * mm});
            skSolve(sketch);
        }
        {
            var Q0;
            Q0 = qSketchRegion(id + "F78", true);
            extrude(context, id + "F79", {"entities" : qUnion([Q0]), "depth" : 304.8 * mm, "offsetDistance" : 25.4 * mm});
        }
        {
            var Q0;
            Q0=sQuery(id+"F0.wireOp",VERTEX,"E24.end");
            var Q1;
            Q1=sQuery(id+"F0.wireOp",EDGE,"E30");
            cPlane(context, id + "F80", {"entities" : qUnion([Q0, Q1]), "cplaneType" : CPlaneType.LINE_POINT, "offset" : 25.4 * mm, "width" : 152.4 * mm, "height" : 152.4 * mm});
        }
        {
            var Q0;
            Q0=qCreatedBy(id+"F80.planeOp",FACE);
            var sketch = newSketch(context, id + "F81", { "sketchPlane" : qUnion([Q0])});
            skCircle(sketch, "E157", {"center": v(1502.58, 0) * mm, "radius": 12.5 * mm});
            skCircle(sketch, "E158", {"center": v(1731.48, 0) * mm, "radius": 12.5 * mm});
            skCircle(sketch, "E159", {"center": v(1960.37, 0) * mm, "radius": 12.5 * mm});
            skCircle(sketch, "E160", {"center": v(2189.27, 0) * mm, "radius": 12.5 * mm});
            skCircle(sketch, "E161", {"center": v(2418.16, 0) * mm, "radius": 12.5 * mm});
            skSolve(sketch);
        }
        {
            var Q0;
            Q0 = qSketchRegion(id + "F81", true);
            extrude(context, id + "F82", {"entities" : qUnion([Q0]), "depth" : 304.8 * mm, "offsetDistance" : 25.4 * mm});
        }
        {
            var Q0;
            Q0=sQuery(id+"F0.wireOp",VERTEX,"E8.end");
            var Q1;
            Q1=sQuery(id+"F0.wireOp",EDGE,"E8");
            cPlane(context, id + "F83", {"entities" : qUnion([Q0, Q1]), "cplaneType" : CPlaneType.LINE_POINT, "offset" : 25.4 * mm, "width" : 152.4 * mm, "height" : 152.4 * mm});
        }
        {
            var Q0;
            Q0=qCreatedBy(id+"F83.planeOp",FACE);
            var sketch = newSketch(context, id + "F84", { "sketchPlane" : qUnion([Q0])});
            skCircle(sketch, "E162", {"center": v(0, 0) * mm, "radius": 12.5 * mm});
            skSolve(sketch);
        }
        {
            var Q0;
            Q0 = qSketchRegion(id + "F84", true);
            extrude(context, id + "F85", {"entities" : qUnion([Q0]), "oppositeDirection" : true, "depth" : 329.9 * mm, "offsetDistance" : 25.4 * mm});
        }
        {
            var Q0;
            Q0=sQuery(id+"F0.wireOp",VERTEX,"E62.MirrorCS.end");
            var Q1;
            Q1=sQuery(id+"F0.wireOp",EDGE,"E64.MirrorCS");
            cPlane(context, id + "F86", {"entities" : qUnion([Q0, Q1]), "cplaneType" : CPlaneType.LINE_POINT, "offset" : 25.4 * mm, "width" : 152.4 * mm, "height" : 152.4 * mm});
        }
        {
            var Q0;
            Q0=qCreatedBy(id+"F86.planeOp",FACE);
            var sketch = newSketch(context, id + "F87", { "sketchPlane" : qUnion([Q0])});
            skCircle(sketch, "E163", {"center": v(1500.92, 0) * mm, "radius": 12.5 * mm});
            skSolve(sketch);
        }
        {
            var Q0;
            Q0 = qSketchRegion(id + "F87", true);
            extrude(context, id + "F88", {"entities" : qUnion([Q0]), "operationType" : NewBodyOperationType.ADD, "oppositeDirection" : true, "depth" : 329.9 * mm, "offsetDistance" : 25.4 * mm});
        }
        {
            var Q0;
            Q0=sQuery(id+"F0.wireOp",VERTEX,"E74.MirrorCS.end");
            var Q1;
            Q1=sQuery(id+"F0.wireOp",EDGE,"E75.MirrorCS");
            cPlane(context, id + "F89", {"entities" : qUnion([Q0, Q1]), "cplaneType" : CPlaneType.LINE_POINT, "offset" : 25.4 * mm, "width" : 152.4 * mm, "height" : 152.4 * mm});
        }
        {
            var Q0;
            Q0=qCreatedBy(id+"F89.planeOp",FACE);
            var sketch = newSketch(context, id + "F90", { "sketchPlane" : qUnion([Q0])});
            skCircle(sketch, "E164", {"center": v(2122.22, 0) * mm, "radius": 12.5 * mm});
            skSolve(sketch);
        }
        {
            var Q0;
            Q0 = qSketchRegion(id + "F90", true);
            extrude(context, id + "F91", {"entities" : qUnion([Q0]), "oppositeDirection" : true, "depth" : 329.9 * mm, "offsetDistance" : 25.4 * mm});
        }
        {
            var Q0;
            Q0=sQuery(id+"F0.wireOp",VERTEX,"E86.MirrorCS.start");
            var Q1;
            Q1=sQuery(id+"F0.wireOp",EDGE,"E87.MirrorCS");
            cPlane(context, id + "F92", {"entities" : qUnion([Q0, Q1]), "cplaneType" : CPlaneType.LINE_POINT, "offset" : 25.4 * mm, "width" : 152.4 * mm, "height" : 152.4 * mm});
        }
        {
            var Q0;
            Q0=qCreatedBy(id+"F92.planeOp",FACE);
            var sketch = newSketch(context, id + "F93", { "sketchPlane" : qUnion([Q0])});
            skCircle(sketch, "E165", {"center": v(1500.62, 0) * mm, "radius": 12.5 * mm});
            skSolve(sketch);
        }
        {
            var Q0;
            Q0 = qSketchRegion(id + "F93", true);
            extrude(context, id + "F94", {"entities" : qUnion([Q0]), "operationType" : NewBodyOperationType.ADD, "oppositeDirection" : true, "depth" : 329.9 * mm, "offsetDistance" : 25.4 * mm});
        }
        {
            var Q0;
            Q0=sQuery(id+"F0.wireOp",VERTEX,"E45.end");
            var Q1;
            Q1=sQuery(id+"F0.wireOp",EDGE,"E45");
            cPlane(context, id + "F95", {"entities" : qUnion([Q0, Q1]), "cplaneType" : CPlaneType.LINE_POINT, "offset" : 25.4 * mm, "width" : 152.4 * mm, "height" : 152.4 * mm});
        }
        {
            var Q0;
            Q0=qCreatedBy(id+"F95.planeOp",FACE);
            var sketch = newSketch(context, id + "F96", { "sketchPlane" : qUnion([Q0])});
            skCircle(sketch, "E166", {"center": v(0, 0) * mm, "radius": 12.5 * mm});
            skSolve(sketch);
        }
        {
            var Q0;
            Q0 = qSketchRegion(id + "F96", true);
            extrude(context, id + "F97", {"entities" : qUnion([Q0]), "operationType" : NewBodyOperationType.ADD, "oppositeDirection" : true, "depth" : 329.9 * mm, "offsetDistance" : 25.4 * mm});
        }
        {
            var Q0;
            Q0=sQuery(id+"F0.wireOp",VERTEX,"E33.end");
            var Q1;
            Q1=sQuery(id+"F0.wireOp",EDGE,"E33");
            cPlane(context, id + "F98", {"entities" : qUnion([Q0, Q1]), "cplaneType" : CPlaneType.LINE_POINT, "offset" : 25.4 * mm, "width" : 152.4 * mm, "height" : 152.4 * mm});
        }
        {
            var Q0;
            Q0=qCreatedBy(id+"F98.planeOp",FACE);
            var sketch = newSketch(context, id + "F99", { "sketchPlane" : qUnion([Q0])});
            skCircle(sketch, "E167", {"center": v(-1499.69, 0) * mm, "radius": 12.5 * mm});
            skSolve(sketch);
        }
        {
            var Q0;
            Q0 = qSketchRegion(id + "F99", true);
            extrude(context, id + "F100", {"entities" : qUnion([Q0]), "operationType" : NewBodyOperationType.ADD, "oppositeDirection" : true, "depth" : 329.9 * mm, "offsetDistance" : 25.4 * mm});
        }
        {
            var Q0;
            Q0=sQuery(id+"F0.wireOp",VERTEX,"E21.end");
            var Q1;
            Q1=sQuery(id+"F0.wireOp",EDGE,"E21");
            cPlane(context, id + "F101", {"entities" : qUnion([Q0, Q1]), "cplaneType" : CPlaneType.LINE_POINT, "offset" : 25.4 * mm, "width" : 152.4 * mm, "height" : 152.4 * mm});
        }
        {
            var Q0;
            Q0=qCreatedBy(id+"F101.planeOp",FACE);
            var sketch = newSketch(context, id + "F102", { "sketchPlane" : qUnion([Q0])});
            skCircle(sketch, "E168", {"center": v(-2121.4, 0) * mm, "radius": 12.5 * mm});
            skSolve(sketch);
        }
        {
            var Q0;
            Q0 = qSketchRegion(id + "F102", true);
            extrude(context, id + "F103", {"entities" : qUnion([Q0]), "operationType" : NewBodyOperationType.ADD, "oppositeDirection" : true, "depth" : 329.9 * mm, "offsetDistance" : 25.4 * mm});
        }
        {
            var Q0;
            Q0=sQuery(id+"F0.wireOp",VERTEX,"E9.end");
            var Q1;
            Q1=sQuery(id+"F0.wireOp",EDGE,"E9");
            cPlane(context, id + "F104", {"entities" : qUnion([Q0, Q1]), "cplaneType" : CPlaneType.LINE_POINT, "offset" : 25.4 * mm, "width" : 152.4 * mm, "height" : 152.4 * mm});
        }
        {
            var Q0;
            Q0=qCreatedBy(id+"F104.planeOp",FACE);
            var sketch = newSketch(context, id + "F105", { "sketchPlane" : qUnion([Q0])});
            skCircle(sketch, "E169", {"center": v(-1500.46, 0) * mm, "radius": 12.5 * mm});
            skSolve(sketch);
        }
        {
            var Q0;
            Q0 = qSketchRegion(id + "F105", true);
            extrude(context, id + "F106", {"entities" : qUnion([Q0]), "operationType" : NewBodyOperationType.ADD, "oppositeDirection" : true, "depth" : 329.9 * mm, "offsetDistance" : 25.4 * mm});
        }
        {
            var Q0;
            Q0=qCreatedBy(makeId("Top.planeOp"),FACE);
            var sketch = newSketch(context, id + "F107", { "sketchPlane" : qUnion([Q0])});
            skCircle(sketch, "E170", {"center": v(0, 0) * mm, "radius": 17.5 * mm});
            skCircle(sketch, "E171", {"center": v(123.72, 306.88) * mm, "radius": 17.5 * mm});
            skCircle(sketch, "E172", {"center": v(-1150.82, 1149.53) * mm, "radius": 17.5 * mm});
            skCircle(sketch, "E173", {"center": v(-843.25, 1276.03) * mm, "radius": 17.5 * mm});
            skCircle(sketch, "E174", {"center": v(-1147.62, 2773.52) * mm, "radius": 17.5 * mm});
            skCircle(sketch, "E175", {"center": v(-843.8, 2646.68) * mm, "radius": 17.5 * mm});
            skCircle(sketch, "E176", {"center": v(0, 3921.82) * mm, "radius": 17.5 * mm});
            skCircle(sketch, "E177", {"center": v(124.88, 3617.72) * mm, "radius": 17.5 * mm});
            skCircle(sketch, "E178", {"center": v(1624.19, 3922.68) * mm, "radius": 17.5 * mm});
            skCircle(sketch, "E179", {"center": v(1496.04, 3616.66) * mm, "radius": 17.5 * mm});
            skCircle(sketch, "E180", {"center": v(2772.36, 2772.98) * mm, "radius": 17.5 * mm});
            skCircle(sketch, "E181", {"center": v(2467.57, 2647.88) * mm, "radius": 17.5 * mm});
            skCircle(sketch, "E182", {"center": v(2772.28, 1151.1) * mm, "radius": 17.5 * mm});
            skCircle(sketch, "E183", {"center": v(2467, 1276.46) * mm, "radius": 17.5 * mm});
            skCircle(sketch, "E184", {"center": v(1497.36, 305.9) * mm, "radius": 17.5 * mm});
            skCircle(sketch, "E185", {"center": v(1624.2, 0) * mm, "radius": 17.5 * mm});
            skSolve(sketch);
        }
        {
            var Q0;
            Q0 = qSketchRegion(id + "F107", true);
            extrude(context, id + "F108", {"entities" : qUnion([Q0]), "oppositeDirection" : true, "depth" : 1524 * mm, "offsetDistance" : 25.4 * mm, "hasSecondDirection" : true, "secondDirectionOppositeDirection" : false, "secondDirectionDepth" : 25.4 * mm});
        }
        {
            var Q0;
            Q0=qCreatedBy(makeId("Top.planeOp"),FACE);
            var sketch = newSketch(context, id + "F109", { "sketchPlane" : qUnion([Q0])});
            skCircle(sketch, "E186", {"center": v(583.43, 0) * mm, "radius": 15 * mm});
            skCircle(sketch, "E187", {"center": v(1040.03, 0) * mm, "radius": 15 * mm});
            skCircle(sketch, "E188", {"center": v(-1148.4, 2189.74) * mm, "radius": 15 * mm});
            skCircle(sketch, "E189", {"center": v(-1148.05, 1733.95) * mm, "radius": 15 * mm});
            skCircle(sketch, "E190", {"center": v(1040.63, 3921.77) * mm, "radius": 15 * mm});
            skCircle(sketch, "E191", {"center": v(583.52, 3921.77) * mm, "radius": 15 * mm});
            skCircle(sketch, "E192", {"center": v(2772.78, 2191.26) * mm, "radius": 15 * mm});
            skCircle(sketch, "E193", {"center": v(2772.53, 1732.7) * mm, "radius": 15 * mm});
            skSolve(sketch);
        }
        {
            var Q0;
            Q0 = qSketchRegion(id + "F109", true);
            extrude(context, id + "F110", {"entities" : qUnion([Q0]), "oppositeDirection" : true, "depth" : 1524 * mm, "offsetDistance" : 25.4 * mm});
        }
        {
            var Q0;
            Q0=sQuery(id+"F0.wireOp",VERTEX,"E17.end");
            var Q1;
            Q1=sQuery(id+"F0.wireOp",EDGE,"E0");
            cPlane(context, id + "F111", {"entities" : qUnion([Q0, Q1]), "cplaneType" : CPlaneType.LINE_POINT, "offset" : 25.4 * mm, "width" : 152.4 * mm, "height" : 152.4 * mm});
        }
        {
            var Q0;
            Q0=qCreatedBy(id+"F111.planeOp",FACE);
            var sketch = newSketch(context, id + "F112", { "sketchPlane" : qUnion([Q0])});
            skCircle(sketch, "E194", {"center": v(0, -252.9) * mm, "radius": 12.5 * mm});
            skCircle(sketch, "E195", {"center": v(0, -507.77) * mm, "radius": 12.5 * mm});
            skCircle(sketch, "E196", {"center": v(0, -760.9) * mm, "radius": 12.5 * mm});
            skCircle(sketch, "E197", {"center": v(0, -1015.2) * mm, "radius": 12.5 * mm});
            skCircle(sketch, "E198", {"center": v(0, -1269.78) * mm, "radius": 12.5 * mm});
            skSolve(sketch);
        }
        {
            var Q0;
            Q0 = qSketchRegion(id + "F112", true);
            extrude(context, id + "F113", {"entities" : qUnion([Q0]), "depth" : 457.2 * mm, "offsetDistance" : 25.4 * mm});
        }
        {
            var Q0;
            Q0=sQuery(id+"F0.wireOp",VERTEX,"E77.MirrorCS.end");
            var Q1;
            Q1=sQuery(id+"F0.wireOp",EDGE,"E6");
            cPlane(context, id + "F114", {"entities" : qUnion([Q0, Q1]), "cplaneType" : CPlaneType.LINE_POINT, "offset" : 25.4 * mm, "width" : 152.4 * mm, "height" : 152.4 * mm});
        }
        {
            var Q0;
            Q0=qCreatedBy(id+"F114.planeOp",FACE);
            var sketch = newSketch(context, id + "F115", { "sketchPlane" : qUnion([Q0])});
            skCircle(sketch, "E199", {"center": v(-1152.55, -249.06) * mm, "radius": 12.5 * mm});
            skCircle(sketch, "E200", {"center": v(-1152.55, -505.2) * mm, "radius": 12.5 * mm});
            skCircle(sketch, "E201", {"center": v(-1149.53, -759.39) * mm, "radius": 12.5 * mm});
            skCircle(sketch, "E202", {"center": v(-1149.53, -1013.8) * mm, "radius": 12.5 * mm});
            skCircle(sketch, "E203", {"center": v(-1152.55, -1264.96) * mm, "radius": 12.5 * mm});
            skSolve(sketch);
        }
        {
            var Q0;
            Q0 = qSketchRegion(id + "F115", true);
            extrude(context, id + "F116", {"entities" : qUnion([Q0]), "depth" : 457.2 * mm, "offsetDistance" : 25.4 * mm});
        }
        {
            var Q0;
            Q0=sQuery(id+"F0.wireOp",VERTEX,"E100.MirrorCS.end");
            var Q1;
            Q1=sQuery(id+"F0.wireOp",EDGE,"E4");
            cPlane(context, id + "F117", {"entities" : qUnion([Q0, Q1]), "cplaneType" : CPlaneType.LINE_POINT, "offset" : 25.4 * mm, "width" : 152.4 * mm, "height" : 152.4 * mm});
        }
        {
            var Q0;
            Q0=qCreatedBy(id+"F117.planeOp",FACE);
            var sketch = newSketch(context, id + "F118", { "sketchPlane" : qUnion([Q0])});
            skCircle(sketch, "E204", {"center": v(-3922.53, -252.41) * mm, "radius": 12.5 * mm});
            skCircle(sketch, "E205", {"center": v(-3922.53, -507.3) * mm, "radius": 12.5 * mm});
            skCircle(sketch, "E206", {"center": v(-3923.23, -759.73) * mm, "radius": 12.5 * mm});
            skCircle(sketch, "E207", {"center": v(-3923.23, -1013.68) * mm, "radius": 12.5 * mm});
            skCircle(sketch, "E208", {"center": v(-3923.23, -1267.64) * mm, "radius": 12.5 * mm});
            skSolve(sketch);
        }
        {
            var Q0;
            Q0 = qSketchRegion(id + "F118", true);
            extrude(context, id + "F119", {"entities" : qUnion([Q0]), "depth" : 457.2 * mm, "offsetDistance" : 25.4 * mm});
        }
        {
            var Q0;
            Q0=sQuery(id+"F0.wireOp",VERTEX,"E41.end");
            var Q1;
            Q1=sQuery(id+"F0.wireOp",EDGE,"E2");
            cPlane(context, id + "F120", {"entities" : qUnion([Q0, Q1]), "cplaneType" : CPlaneType.LINE_POINT, "offset" : 25.4 * mm, "width" : 152.4 * mm, "height" : 152.4 * mm});
        }
        {
            var Q0;
            Q0=qCreatedBy(id+"F120.planeOp",FACE);
            var sketch = newSketch(context, id + "F121", { "sketchPlane" : qUnion([Q0])});
            skCircle(sketch, "E209", {"center": v(-2775.3, -251.54) * mm, "radius": 12.5 * mm});
            skCircle(sketch, "E210", {"center": v(-2775.3, -505.95) * mm, "radius": 12.5 * mm});
            skCircle(sketch, "E211", {"center": v(-2775.3, -760.36) * mm, "radius": 12.5 * mm});
            skCircle(sketch, "E212", {"center": v(-2775.3, -1013.03) * mm, "radius": 12.5 * mm});
            skCircle(sketch, "E213", {"center": v(-2775.3, -1267.44) * mm, "radius": 12.5 * mm});
            skSolve(sketch);
        }
        {
            var Q0;
            Q0 = qSketchRegion(id + "F121", true);
            extrude(context, id + "F122", {"entities" : qUnion([Q0]), "depth" : 457.2 * mm, "offsetDistance" : 25.4 * mm});
        }
    });
